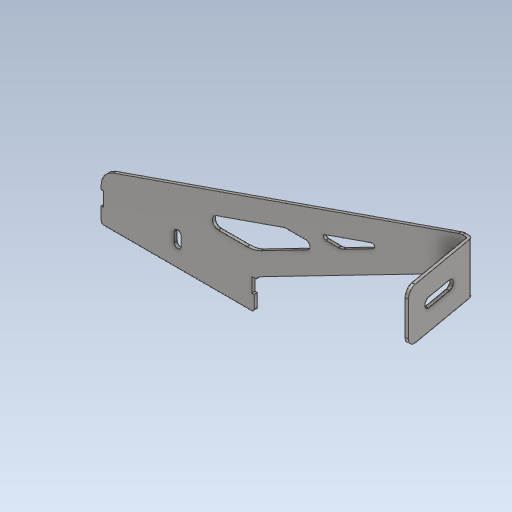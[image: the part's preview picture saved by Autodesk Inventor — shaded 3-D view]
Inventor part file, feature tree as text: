
AUTODESK INVENTOR PART (.ipt)
format: ipt  version: 2020 (Build 240168000, 168)  size: 199,680 bytes
history: native  units: mm
features: other x4, sketch x1, plane x1
ambient origin geometry x8: Origin, YZ Plane, XZ Plane, XY Plane, X Axis, Y Axis, Z Axis, Center Point
bodies: Body1 (feature_tree)
feature tree (6):
  other  "白鐵-吊架-長(R)(#11.02).ipt"
  other  "實體1::白鐵-吊架-長(R)(#11.02).ipt"
  other  "標籤特徵1"
  sketch  "草圖1"
  plane  "工作平面1"
  other  "實體1"
